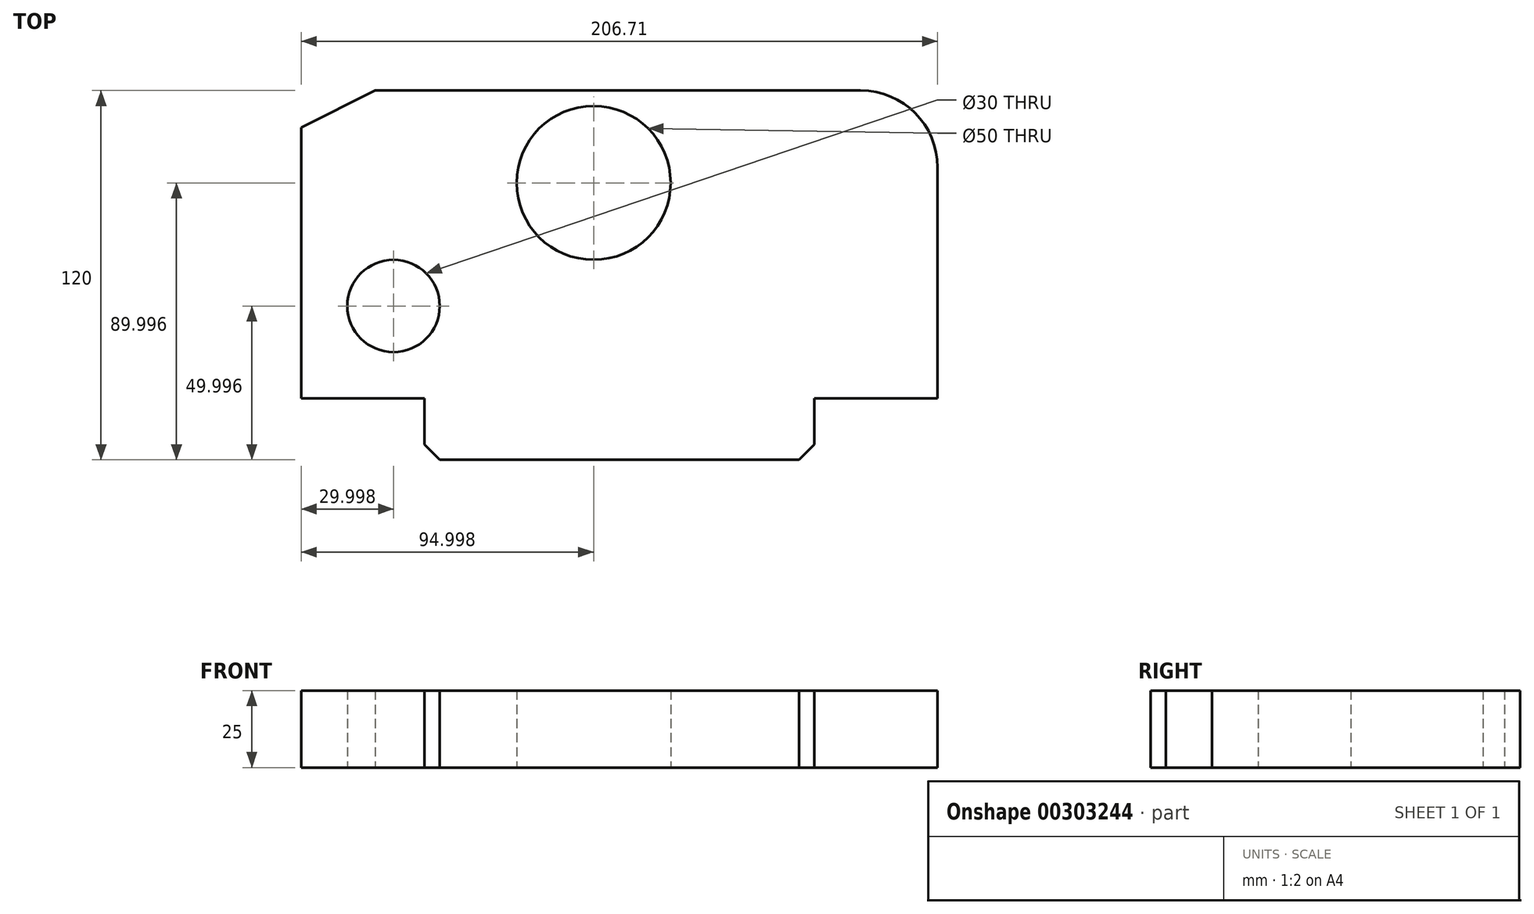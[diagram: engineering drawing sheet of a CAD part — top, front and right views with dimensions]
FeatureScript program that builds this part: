
annotation { "Feature Type Name" : "Feature", "Feature Type Description" : "" }
export const myFeature = defineFeature(function(context is Context, id is Id, definition is map)
    precondition{}
    {
        {
            var Q0;
            Q0=qCreatedBy(makeId("Top.planeOp"),FACE);
            var sketch = newSketch(context, id + "F0", { "sketchPlane" : qUnion([Q0])});
            skLineSegment(sketch, "E0", {"start": v(-47.35, 50.98) * mm, "end": v(-47.35, -37.02) * mm});
            skLineSegment(sketch, "E1", {"start": v(-23.35, 62.98) * mm, "end": v(-47.35, 50.98) * mm});
            skLineSegment(sketch, "E2", {"start": v(-23.35, 62.98) * mm, "end": v(134.36, 62.98) * mm});
            skLineSegment(sketch, "E3", {"start": v(159.36, 37.98) * mm, "end": v(159.36, -37.02) * mm});
            skLineSegment(sketch, "E4", {"start": v(159.36, -37.02) * mm, "end": v(119.36, -37.02) * mm});
            skLineSegment(sketch, "E5", {"start": v(119.36, -37.02) * mm, "end": v(119.36, -57.02) * mm});
            skLineSegment(sketch, "E6", {"start": v(-47.35, -37.02) * mm, "end": v(-7.35, -37.02) * mm});
            skLineSegment(sketch, "E7", {"start": v(-7.35, -37.02) * mm, "end": v(-7.35, -57.02) * mm});
            skLineSegment(sketch, "E8", {"start": v(-7.35, -57.02) * mm, "end": v(119.36, -57.02) * mm});
            skLineSegment(sketch, "E9", {"start": v(-47.35, -37.02) * mm, "end": v(-17.35, -37.02) * mm});
            skLineSegment(sketch, "E10", {"start": v(-47.35, -37.02) * mm, "end": v(-47.35, -7.02) * mm});
            skCircle(sketch, "E11", {"center": v(-17.35, -7.02) * mm, "radius": 15 * mm});
            skCircle(sketch, "E12", {"center": v(47.65, 32.98) * mm, "radius": 25 * mm});
            skPoint(sketch, "E13.visualSharp", {"position": v(159.36, 62.98) * mm});
            skArc(sketch, "E13.filletArc", {"start": v(159.36, 37.98) * mm, "mid": v(152.04, 55.65) * mm, "end": v(134.36, 62.98) * mm});
            skSolve(sketch);
        }
        {
            var Q0;
            Q0 = qSketchRegion(id + "F0", true);
            extrude(context, id + "F1", {"entities" : qUnion([Q0]), "depth" : 25 * mm});
        }
        {
            var Q0;
            Q0=makeQuery(id+"F1.opExtrude","SWEPT_EDGE",EDGE,{"disambiguationData":[OSD([sQuery(id+"F0.wireOp",EDGE,"E7"),sQuery(id+"F0.wireOp",EDGE,"E8")])]});
            var Q1;
            Q1=makeQuery(id+"F1.opExtrude","SWEPT_EDGE",EDGE,{"disambiguationData":[OSD([sQuery(id+"F0.wireOp",EDGE,"E5"),sQuery(id+"F0.wireOp",EDGE,"E8")])]});
            chamfer(context, id + "F2", {"entities" : qUnion([Q0, Q1]), "width" : 5 * mm, "tangentPropagation" : true});
        }
    });
